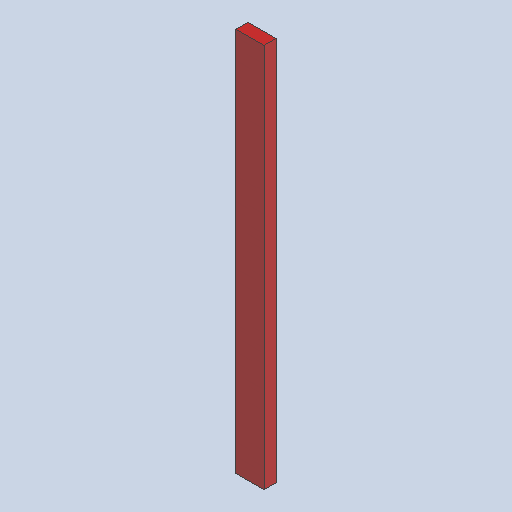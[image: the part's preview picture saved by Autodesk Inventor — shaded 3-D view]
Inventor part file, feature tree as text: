
AUTODESK INVENTOR PART (.ipt)
format: ipt  version: 2025 (Build 290162000, 162)  size: 88,576 bytes
history: native  units: in
note: dims shown in document units (in); Inventor stores cm internally (conversion verified against a paired STEP export)
features: other x4, sketch x1
ambient origin geometry x8: Origin, YZ Plane, XZ Plane, XY Plane, X Axis, Y Axis, Z Axis, Center Point
bodies: Solid1 (feature_tree)
feature tree (5):
  other  "8'x2x4_MIR.ipt"
  other  "Solid1::8'x2x4_MIR.ipt"
  other  "TaggingFeature1"
  sketch  "Sketch1"  dims[d0=0.3937in]
  other  "Finish1"
